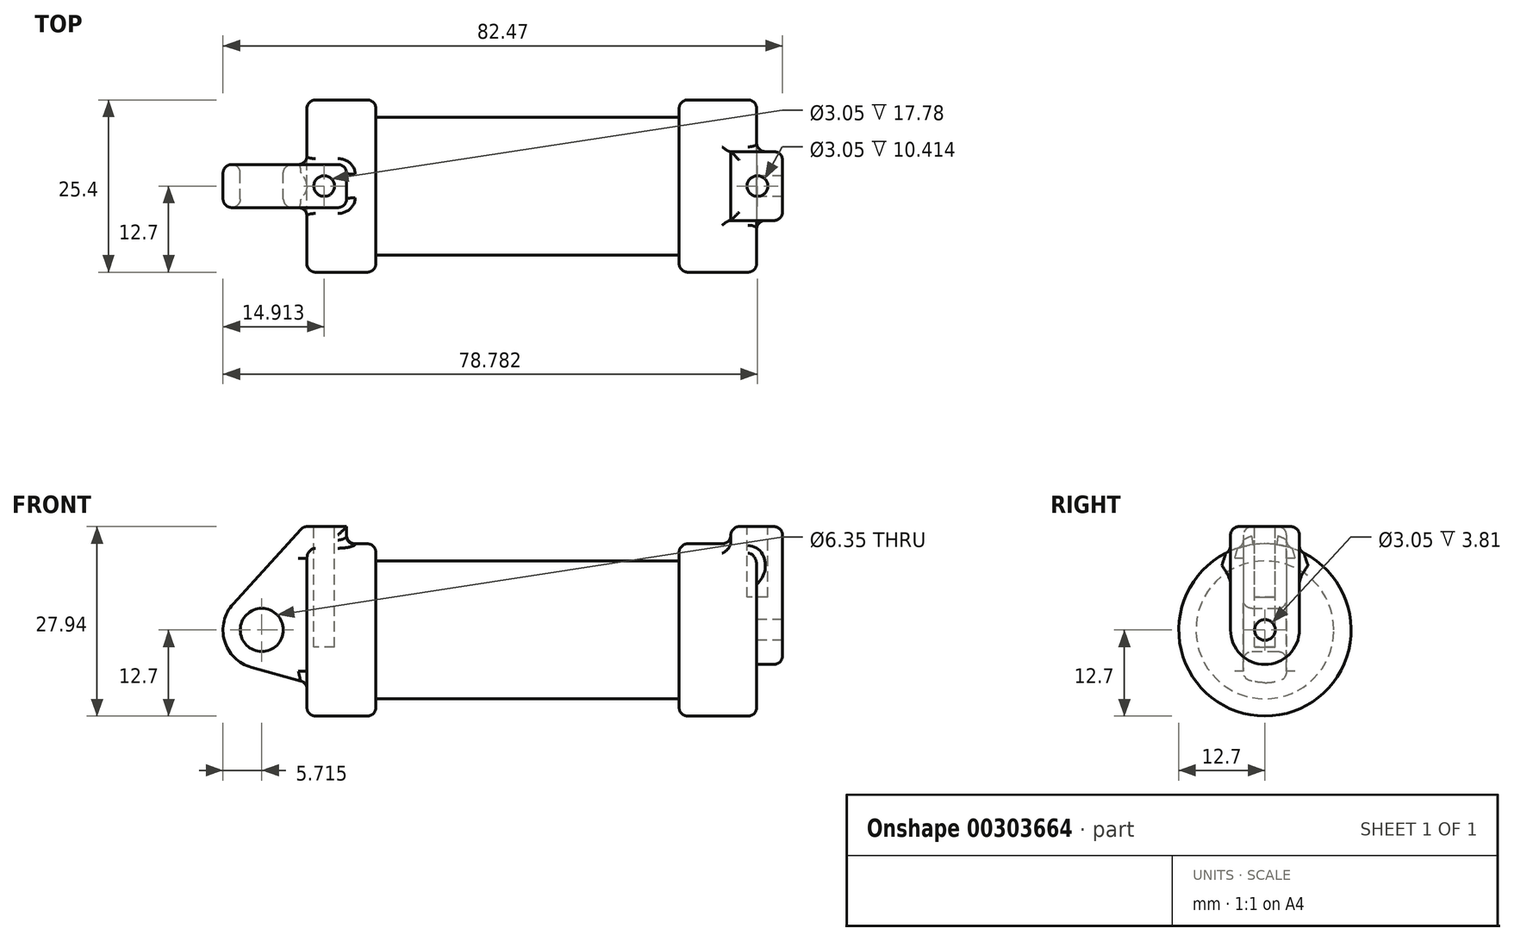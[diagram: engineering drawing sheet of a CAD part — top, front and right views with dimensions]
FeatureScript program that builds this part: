
annotation { "Feature Type Name" : "Feature", "Feature Type Description" : "" }
export const myFeature = defineFeature(function(context is Context, id is Id, definition is map)
    precondition{}
    {
        {
            var Q0;
            Q0=qCreatedBy(makeId("Front.planeOp"),FACE);
            var sketch = newSketch(context, id + "F0", { "sketchPlane" : qUnion([Q0])});
            skLineSegment(sketch, "E0", {"start": v(0, 0) * mm, "end": v(0, 12.7) * mm});
            skLineSegment(sketch, "E1", {"start": v(0, 12.7) * mm, "end": v(10.16, 12.7) * mm});
            skLineSegment(sketch, "E2", {"start": v(10.16, 12.7) * mm, "end": v(10.16, 10.16) * mm});
            skLineSegment(sketch, "E3", {"start": v(10.16, 10.16) * mm, "end": v(56.13, 10.16) * mm});
            skLineSegment(sketch, "E4", {"start": v(56.13, 10.16) * mm, "end": v(56.13, 12.7) * mm});
            skLineSegment(sketch, "E5", {"start": v(56.13, 12.7) * mm, "end": v(66.3, 12.7) * mm});
            skLineSegment(sketch, "E6", {"start": v(66.3, 12.7) * mm, "end": v(66.3, 0) * mm});
            skLineSegment(sketch, "E7", {"start": v(66.3, 0) * mm, "end": v(0, 0) * mm});
            skLineSegment(sketch, "E8", {"start": v(5.84, 15.24) * mm, "end": v(-0.5, 15.24) * mm});
            skLineSegment(sketch, "E9", {"start": v(-0.5, 15.24) * mm, "end": v(-10.88, 3.85) * mm});
            skLineSegment(sketch, "E10", {"start": v(0, 0) * mm, "end": v(-6.65, 0) * mm});
            skCircle(sketch, "E11", {"center": v(-6.65, 0) * mm, "radius": 5.72 * mm});
            skCircle(sketch, "E12", {"center": v(-6.65, 0) * mm, "radius": 3.18 * mm});
            skLineSegment(sketch, "E13", {"start": v(5.84, 15.24) * mm, "end": v(5.84, -9.4) * mm});
            skLineSegment(sketch, "E14", {"start": v(5.84, -9.4) * mm, "end": v(-8.18, -5.5) * mm});
            skCircle(sketch, "E15", {"center": v(-6.65, 0) * mm, "radius": 1.52 * mm});
            skSolve(sketch);
        }
        {
            var Q0;
            {var subQ0=sQuery(id+"F0.wireOp",EDGE,"E2");Q0=makeQuery(id+"F0.imprint","IMPRINT",FACE,{"disambiguationData":[TD([[makeQuery(id+"F0.imprint","IMPRINT",EDGE,{"derivedFrom":subQ0}),-1.0]])]});}
            var Q1;
            {var subQ0=sQuery(id+"F0.wireOp",EDGE,"E0");Q1=makeQuery(id+"F0.imprint","IMPRINT",FACE,{"disambiguationData":[TD([[makeQuery(id+"F0.imprint","IMPRINT",EDGE,{"derivedFrom":subQ0}),-1.0]])]});}
            var Q2;
            Q2=sQuery(id+"F0.wireOp",EDGE,"E7");
            revolve(context, id + "F1", {"entities" : qUnion([Q0, Q1]), "axis" : qUnion([Q2]), "revolveType" : RevolveType.FULL});
        }
        {
            var Q0;
            {var subQ0=sQuery(id+"F0.wireOp",EDGE,"E0");Q0=makeQuery(id+"F0.imprint","IMPRINT",FACE,{"disambiguationData":[TD([[makeQuery(id+"F0.imprint","IMPRINT",EDGE,{"derivedFrom":subQ0}),-1.0]])]});}
            var Q1;
            {var subQ1=sQuery(id+"F0.wireOp",EDGE,"E0");Q1=makeQuery(id+"F0.imprint","IMPRINT",FACE,{"disambiguationData":[TD([[makeQuery(id+"F0.imprint","IMPRINT",EDGE,{"derivedFrom":subQ1}),1.0]])]});}
            var Q2;
            Q2=makeQuery(id+"F0.imprint","IMPRINT",FACE,{"disambiguationData":[TD([[makeQuery(id+"F0.imprint","IMPRINT",EDGE,{"derivedFrom":sQuery(id+"F0.wireOp",EDGE,"E12")}),-1.0]])]});
            var Q3;
            {var subQ0=sQuery(id+"F0.wireOp",EDGE,"E14");Q3=makeQuery(id+"F0.imprint","IMPRINT",FACE,{"disambiguationData":[TD([[makeQuery(id+"F0.imprint","IMPRINT",EDGE,{"derivedFrom":subQ0}),-1.0]])]});}
            extrude(context, id + "F2", {"entities" : qUnion([Q0, Q1, Q2, Q3]), "operationType" : NewBodyOperationType.ADD, "endBound" : BoundingType.SYMMETRIC, "depth" : 6.35 * mm});
        }
        {
            var Q0;
            Q0=makeQuery(id+"F1.opRevolve","SWEPT_FACE",FACE,{"disambiguationData":[OSD([sQuery(id+"F0.wireOp",EDGE,"E6")])]});
            var sketch = newSketch(context, id + "F3", { "sketchPlane" : qUnion([Q0])});
            skCircle(sketch, "E16", {"center": v(0, 0) * mm, "radius": 1.52 * mm});
            skCircle(sketch, "E17", {"center": v(0, 0) * mm, "radius": 5.08 * mm});
            skLineSegment(sketch, "E18", {"start": v(-5.08, 0) * mm, "end": v(-5.08, 15.24) * mm});
            skLineSegment(sketch, "E19", {"start": v(5.08, 0) * mm, "end": v(5.08, 15.24) * mm});
            skLineSegment(sketch, "E20", {"start": v(-5.08, 15.24) * mm, "end": v(5.08, 15.24) * mm});
            skSolve(sketch);
        }
        {
            var Q0;
            Q0=makeQuery(id+"F1.opRevolve","SWEPT_FACE",FACE,{"disambiguationData":[OSD([sQuery(id+"F0.wireOp",EDGE,"E4")])]});
            extrude(context, id + "F4", {"entities" : qUnion([Q0]), "operationType" : NewBodyOperationType.ADD, "depth" : 1.27 * mm});
        }
        {
            var Q0;
            Q0=makeQuery(id+"F3.imprint","IMPRINT",FACE,{"disambiguationData":[TD([[makeQuery(id+"F3.imprint","IMPRINT",EDGE,{"derivedFrom":sQuery(id+"F3.wireOp",EDGE,"E16")}),-1.0]])]});
            var Q1;
            {var subQ0=sQuery(id+"F3.wireOp",EDGE,"E18");var subQ1=sQuery(id+"F3.wireOp",EDGE,"E17");var subQ2=makeQuery(id+"F3.imprint","INTERSECT",VERTEX,{"derivedFrom":[subQ1,subQ0]});Q1=makeQuery(id+"F3.imprint","IMPRINT",FACE,{"disambiguationData":[TD([[makeQuery(id+"F3.imprint","IMPRINT",EDGE,{"disambiguationData":[TD([[subQ2,1.0]])],"derivedFrom":subQ1}),-1.0]])]});}
            var Q2;
            {var subQ0=sQuery(id+"F3.wireOp",EDGE,"E20");Q2=makeQuery(id+"F3.imprint","IMPRINT",FACE,{"disambiguationData":[TD([[makeQuery(id+"F3.imprint","IMPRINT",EDGE,{"derivedFrom":subQ0}),-1.0]])]});}
            extrude(context, id + "F5", {"entities" : qUnion([Q0, Q1, Q2]), "operationType" : NewBodyOperationType.ADD, "endBound" : BoundingType.SYMMETRIC, "depth" : 7.62 * mm});
        }
        {
            var Q0;
            Q0=makeQuery(id+"F2.opExtrude","SWEPT_FACE",FACE,{"disambiguationData":[OSD([sQuery(id+"F0.wireOp",EDGE,"E8")])]});
            var sketch = newSketch(context, id + "F6", { "sketchPlane" : qUnion([Q0])});
            skCircle(sketch, "E21", {"center": v(2.54, 0) * mm, "radius": 1.52 * mm});
            skPoint(sketch, "E21.centerSnap0", {"position": v(-0.5, 0) * mm});
            skSolve(sketch);
        }
        {
            var Q0;
            Q0=makeQuery(id+"F5.opExtrude","SWEPT_FACE",FACE,{"disambiguationData":[OSD([sQuery(id+"F3.wireOp",EDGE,"E20")])]});
            var sketch = newSketch(context, id + "F7", { "sketchPlane" : qUnion([Q0])});
            skCircle(sketch, "E22", {"center": v(66.41, 0) * mm, "radius": 1.52 * mm});
            skPoint(sketch, "E22.centerSnap0", {"position": v(62.48, 0) * mm});
            skSolve(sketch);
        }
        {
            var Q0;
            Q0=makeQuery(id+"F6.imprint","IMPRINT",FACE,{"disambiguationData":[TD([[makeQuery(id+"F6.imprint","IMPRINT",EDGE,{"derivedFrom":sQuery(id+"F6.wireOp",EDGE,"E21")}),1.0]])]});
            extrude(context, id + "F8", {"entities" : qUnion([Q0]), "operationType" : NewBodyOperationType.REMOVE, "oppositeDirection" : true, "depth" : 17.78 * mm});
        }
        {
            var Q0;
            Q0=makeQuery(id+"F7.imprint","IMPRINT",FACE,{"disambiguationData":[TD([[makeQuery(id+"F7.imprint","IMPRINT",EDGE,{"derivedFrom":sQuery(id+"F7.wireOp",EDGE,"E22")}),1.0]])]});
            extrude(context, id + "F9", {"entities" : qUnion([Q0]), "operationType" : NewBodyOperationType.REMOVE, "oppositeDirection" : true, "depth" : 10.4 * mm});
        }
        {
            var Q0;
            Q0=makeQuery(id+"F2.opExtrude","CAP_EDGE",EDGE,{"disambiguationData":[OSD([sQuery(id+"F0.wireOp",EDGE,"E12")])],"isStart":false});
            var Q1;
            Q1=makeQuery(id+"F5.opExtrude","CAP_EDGE",EDGE,{"disambiguationData":[OSD([sQuery(id+"F3.wireOp",EDGE,"E17")])],"isStart":false});
            var Q2;
            Q2=makeQuery(id+"F5.opExtrude","CAP_EDGE",EDGE,{"disambiguationData":[OSD([sQuery(id+"F3.wireOp",EDGE,"E19")])],"isStart":false});
            var Q3;
            Q3=makeQuery(id+"F2.opExtrude","CAP_EDGE",EDGE,{"disambiguationData":[OSD([sQuery(id+"F0.wireOp",EDGE,"E9")])],"isStart":false});
            var Q4;
            Q4=makeQuery(id+"F2.opExtrude","CAP_EDGE",EDGE,{"disambiguationData":[OSD([sQuery(id+"F0.wireOp",EDGE,"E11")])],"isStart":false});
            var Q5;
            Q5=makeQuery(id+"F2.opExtrude","CAP_EDGE",EDGE,{"disambiguationData":[OSD([sQuery(id+"F0.wireOp",EDGE,"E14")])],"isStart":false});
            var Q6;
            Q6=makeQuery(id+"F2.opExtrude","CAP_FACE",FACE,{"disambiguationData":[OSD([sQuery(id+"F0.wireOp",EDGE,"E8"),sQuery(id+"F0.wireOp",EDGE,"E9"),sQuery(id+"F0.wireOp",EDGE,"E11"),sQuery(id+"F0.wireOp",EDGE,"E12"),sQuery(id+"F0.wireOp",EDGE,"E13"),sQuery(id+"F0.wireOp",EDGE,"E14")])],"isStart":false});
            var Q7;
            Q7=makeQuery(id+"F2.opExtrude","CAP_FACE",FACE,{"disambiguationData":[OSD([sQuery(id+"F0.wireOp",EDGE,"E8"),sQuery(id+"F0.wireOp",EDGE,"E9"),sQuery(id+"F0.wireOp",EDGE,"E11"),sQuery(id+"F0.wireOp",EDGE,"E12"),sQuery(id+"F0.wireOp",EDGE,"E13"),sQuery(id+"F0.wireOp",EDGE,"E14")])],"isStart":true});
            var Q8;
            Q8=makeQuery(id+"F2.opExtrude","SWEPT_FACE",FACE,{"disambiguationData":[OSD([sQuery(id+"F0.wireOp",EDGE,"E9")])]});
            var Q9;
            Q9=makeQuery(id+"F2.opExtrude","SWEPT_FACE",FACE,{"disambiguationData":[OSD([sQuery(id+"F0.wireOp",EDGE,"E11")])]});
            var Q10;
            Q10=makeQuery(id+"F1.opRevolve","SWEPT_FACE",FACE,{"disambiguationData":[OSD([sQuery(id+"F0.wireOp",EDGE,"E1")])]});
            var Q11;
            {var subQ0=sQuery(id+"F0.wireOp",EDGE,"E5");Q11=makeQuery(id+"F4.boolean.opBoolean","MERGE",FACE,{"derivedFrom":[makeQuery(id+"F1.opRevolve","SWEPT_FACE",FACE,{"disambiguationData":[OSD([subQ0])]}),makeQuery(id+"F4.opExtrude","SWEPT_FACE",FACE,{"disambiguationData":[OSD([sQuery(id+"F0.wireOp",EDGE,"E4"),subQ0])]})]});}
            var Q12;
            Q12=makeQuery(id+"F5.opExtrude","CAP_EDGE",EDGE,{"disambiguationData":[OSD([sQuery(id+"F3.wireOp",EDGE,"E20")])],"isStart":false});
            var Q13;
            Q13=makeQuery(id+"F5.opExtrude","SWEPT_EDGE",EDGE,{"disambiguationData":[OSD([sQuery(id+"F3.wireOp",EDGE,"E18"),sQuery(id+"F3.wireOp",EDGE,"E20")])]});
            var Q14;
            Q14=makeQuery(id+"F5.opExtrude","CAP_EDGE",EDGE,{"disambiguationData":[OSD([sQuery(id+"F3.wireOp",EDGE,"E20")])],"isStart":true});
            var Q15;
            Q15=makeQuery(id+"F5.opExtrude","SWEPT_EDGE",EDGE,{"disambiguationData":[OSD([sQuery(id+"F3.wireOp",EDGE,"E19"),sQuery(id+"F3.wireOp",EDGE,"E20")])]});
            fillet(context, id + "F10", {"entities" : qUnion([Q0, Q1, Q2, Q3, Q4, Q5, Q6, Q7, Q8, Q9, Q10, Q11, Q12, Q13, Q14, Q15]), "radius" : 1.27 * mm, "tangentPropagation" : true, "allowEdgeOverflow" : false});
        }
    });
